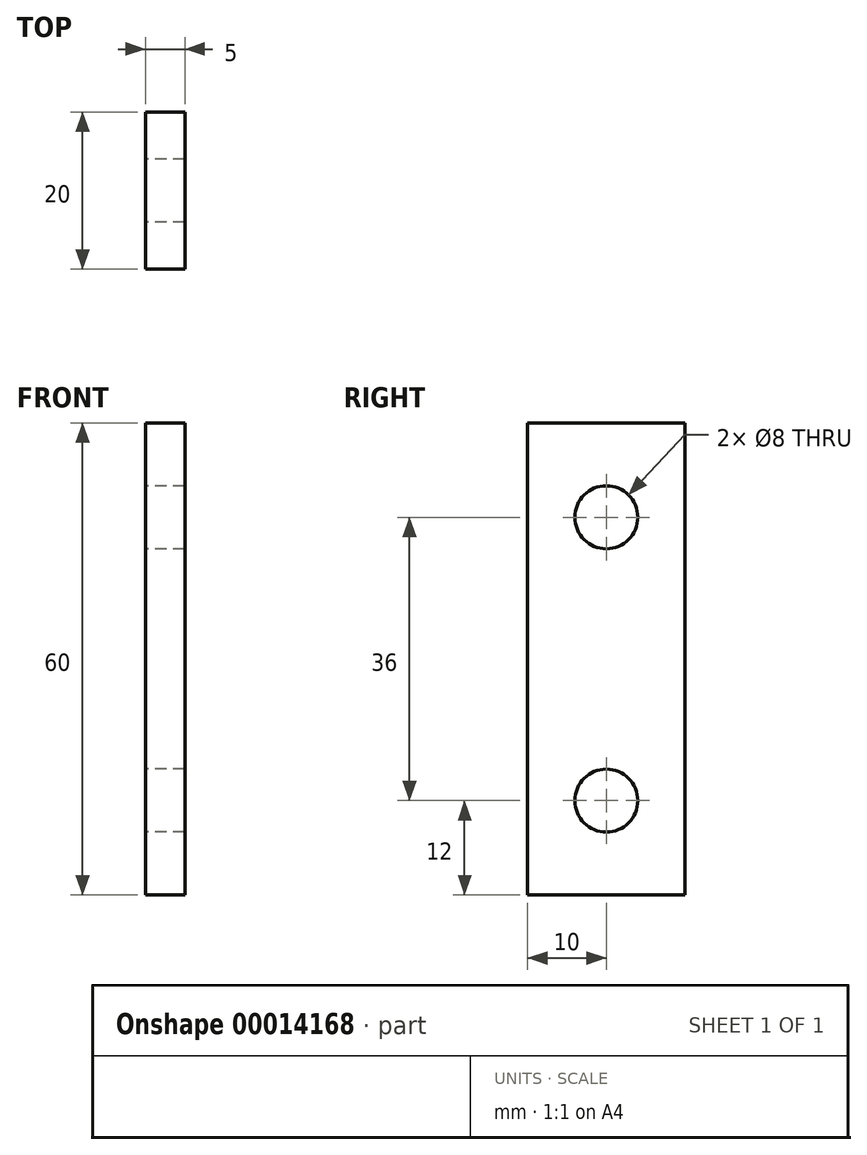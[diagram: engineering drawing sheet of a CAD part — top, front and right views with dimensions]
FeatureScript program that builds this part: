
annotation { "Feature Type Name" : "Feature", "Feature Type Description" : "" }
export const myFeature = defineFeature(function(context is Context, id is Id, definition is map)
    precondition{}
    {
        {
            var Q0;
            Q0=qCreatedBy(makeId("Right.planeOp"),FACE);
            var sketch = newSketch(context, id + "F0", { "sketchPlane" : qUnion([Q0])});
            skLineSegment(sketch, "E0.rect.bottom", {"start": v(-10, 30) * mm, "end": v(10, 30) * mm});
            skLineSegment(sketch, "E0.rect.top", {"start": v(-10, -30) * mm, "end": v(10, -30) * mm});
            skLineSegment(sketch, "E0.rect.left", {"start": v(-10, 30) * mm, "end": v(-10, -30) * mm});
            skLineSegment(sketch, "E0.rect.right", {"start": v(10, 30) * mm, "end": v(10, -30) * mm});
            skPoint(sketch, "E0.rect.middle", {"position": v(0, 0) * mm});
            skLineSegment(sketch, "E1", {"start": v(0, 18) * mm, "end": v(0, -18) * mm, "construction": true});
            skLineSegment(sketch, "E2", {"start": v(-13.22, 0) * mm, "end": v(9.63, 0) * mm, "construction": true});
            skCircle(sketch, "E3", {"center": v(0, 18) * mm, "radius": 4 * mm});
            skCircle(sketch, "E4", {"center": v(0, -18) * mm, "radius": 4 * mm});
            skSolve(sketch);
        }
        {
            var Q0;
            Q0 = qSketchRegion(id + "F0", true);
            extrude(context, id + "F1", {"entities" : qUnion([Q0]), "depth" : 5 * mm});
        }
    });
